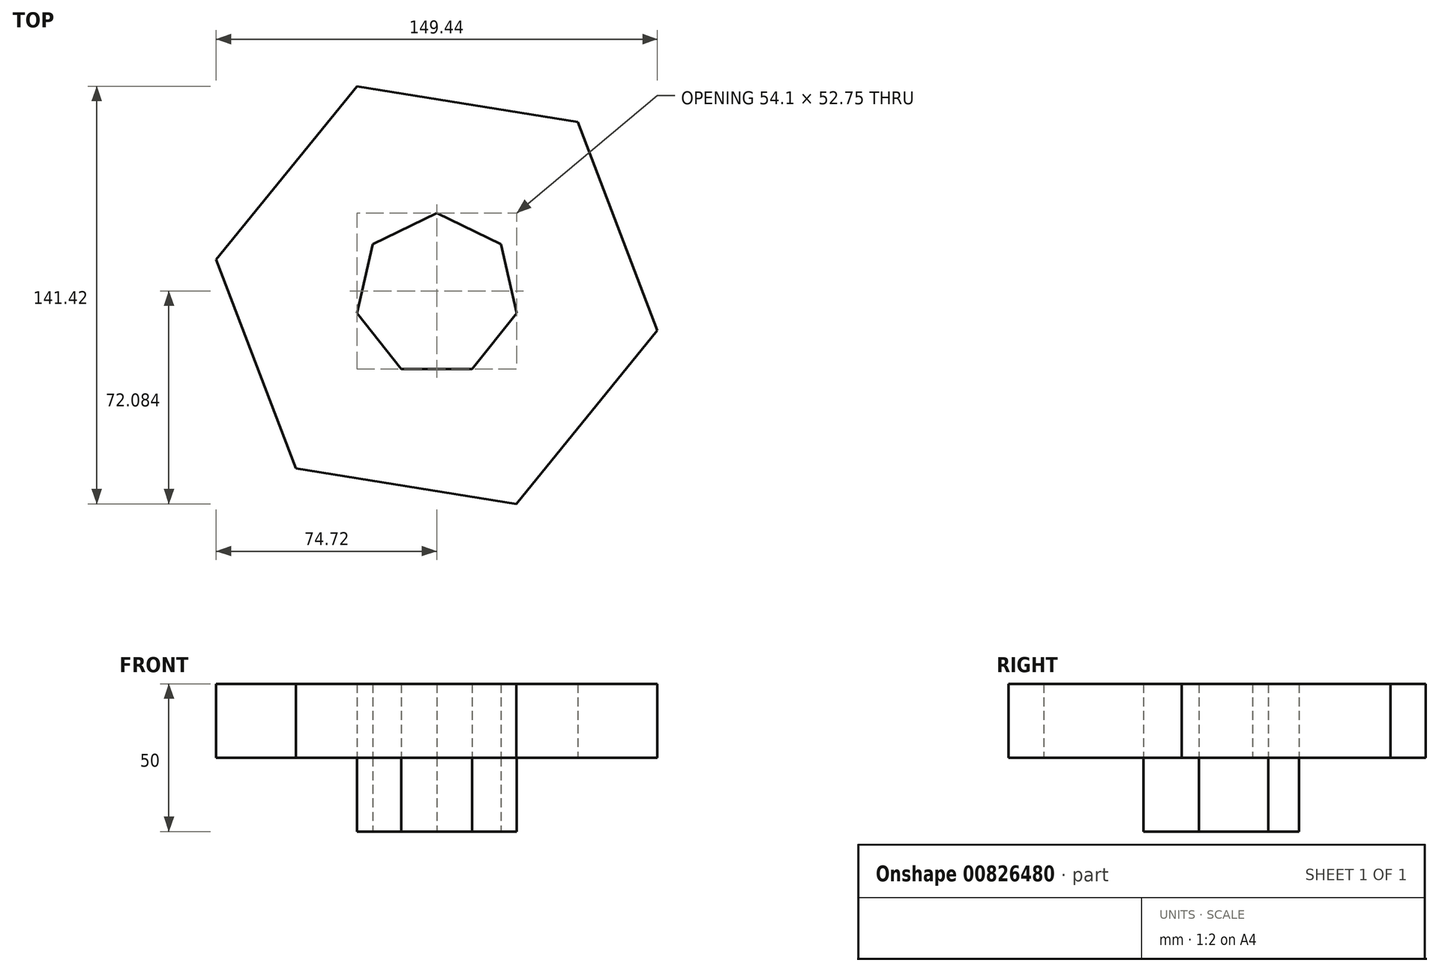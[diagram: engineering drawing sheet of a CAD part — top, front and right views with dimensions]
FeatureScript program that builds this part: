
annotation { "Feature Type Name" : "Feature", "Feature Type Description" : "" }
export const myFeature = defineFeature(function(context is Context, id is Id, definition is map)
    precondition{}
    {
        {
            var Q0;
            Q0=qCreatedBy(makeId("Top.planeOp"),FACE);
            var sketch = newSketch(context, id + "F0", { "sketchPlane" : qUnion([Q0])});
            skCircle(sketch, "E0.cCircle", {"center": v(0, 0) * mm, "radius": 25 * mm, "construction": true});
            skLineSegment(sketch, "E0.0", {"start": v(12.04, -25) * mm, "end": v(-12.04, -25) * mm});
            skLineSegment(sketch, "E0.1", {"start": v(-12.04, -25) * mm, "end": v(-27.05, -6.17) * mm});
            skLineSegment(sketch, "E0.2", {"start": v(-27.05, -6.17) * mm, "end": v(-21.7, 17.3) * mm});
            skLineSegment(sketch, "E0.3", {"start": v(-21.7, 17.3) * mm, "end": v(0, 27.75) * mm});
            skLineSegment(sketch, "E0.4", {"start": v(0, 27.75) * mm, "end": v(21.7, 17.3) * mm});
            skLineSegment(sketch, "E0.5", {"start": v(21.7, 17.3) * mm, "end": v(27.05, -6.17) * mm});
            skLineSegment(sketch, "E0.6", {"start": v(27.05, -6.17) * mm, "end": v(12.04, -25) * mm});
            skPoint(sketch, "E0.0.midPoint", {"position": v(0, -25) * mm});
            skSolve(sketch);
        }
        {
            var Q0;
            Q0=makeQuery(id+"F0.imprint","IMPRINT",FACE,{"disambiguationData":[TD([[makeQuery(id+"F0.imprint","IMPRINT",EDGE,{"derivedFrom":sQuery(id+"F0.wireOp",EDGE,"E0.0")}),-1.0]])]});
            extrude(context, id + "F1", {"entities" : qUnion([Q0]), "depth" : 25 * mm, "offsetDistance" : 25 * mm});
        }
        {
            var Q0;
            Q0=makeQuery(id+"F1.opExtrude","CAP_FACE",FACE,{"disambiguationData":[OSD([sQuery(id+"F0.wireOp",EDGE,"E0.0"),sQuery(id+"F0.wireOp",EDGE,"E0.1"),sQuery(id+"F0.wireOp",EDGE,"E0.2"),sQuery(id+"F0.wireOp",EDGE,"E0.3"),sQuery(id+"F0.wireOp",EDGE,"E0.4"),sQuery(id+"F0.wireOp",EDGE,"E0.5"),sQuery(id+"F0.wireOp",EDGE,"E0.6")])],"isStart":false});
            var sketch = newSketch(context, id + "F2", { "sketchPlane" : qUnion([Q0])});
            skCircle(sketch, "E1.cCircle", {"center": v(0, 0) * mm, "radius": 65.54 * mm, "construction": true});
            skLineSegment(sketch, "E1.0", {"start": v(-74.72, 12) * mm, "end": v(-26.97, 70.71) * mm});
            skLineSegment(sketch, "E1.1", {"start": v(-26.97, 70.71) * mm, "end": v(47.76, 58.71) * mm});
            skLineSegment(sketch, "E1.2", {"start": v(47.76, 58.71) * mm, "end": v(74.72, -12) * mm});
            skLineSegment(sketch, "E1.3", {"start": v(74.72, -12) * mm, "end": v(26.97, -70.71) * mm});
            skLineSegment(sketch, "E1.4", {"start": v(26.97, -70.71) * mm, "end": v(-47.76, -58.71) * mm});
            skLineSegment(sketch, "E1.5", {"start": v(-47.76, -58.71) * mm, "end": v(-74.72, 12) * mm});
            skPoint(sketch, "E1.0.midPoint", {"position": v(-50.84, 41.36) * mm});
            skSolve(sketch);
        }
        {
            var Q0;
            Q0=makeQuery(id+"F2.imprint","IMPRINT",FACE,{"disambiguationData":[TD([[makeQuery(id+"F2.imprint","IMPRINT",EDGE,{"derivedFrom":sQuery(id+"F2.wireOp",EDGE,"E1.0")}),-1.0]])]});
            extrude(context, id + "F3", {"entities" : qUnion([Q0]), "depth" : 25 * mm, "offsetDistance" : 25 * mm});
        }
    });
